SOLIDWORKS PART (.sldprt)
format: sldprt  version: not decoded by parser v0  size: 238,592 bytes
history: native  units: mm
features: sketch x4, fillet x4, extrude x3, plane x2, material x1, shell x1, cut_extrude x1 (+13 scaffold rows collapsed)
feature tree (29):
  scaffold x13  (default folders/planes/origin — collapsed)
  material  "ABS"
  plane  "Plane1"
  sketch  "Sketch1"  dims[D1=50.0mm D2=110.0mm]
  extrude  "Boss-Extrude1"  Depth=5.08mm
  shell  "Shell1"  Thickness=3.048mm
  sketch  "Sketch4"  dims[c1.D1=5.2832mm c1.D2=5.2832mm c2.D1=93.0mm c2.D2=2.64mm c2.D3=3.5mm c2.D4=2.64mm c2.D5=2.64mm c3.D1=3.5mm c3.D2=3.5mm c3.D4=3.5mm]
  cut_extrude  "Cut-Extrude1"  [1 undecoded]
  fillet  "Fillet1"  Radius=3.5052mm
  plane  "Plane2"
  sketch  "Sketch6"  dims[D1=2.032mm]
  extrude  "Boss-Extrude3"  Depth=2.54mm
  sketch  "Sketch7"
  extrude  "Boss-Extrude4"  Depth=1.524mm
  fillet  "Fillet2"  Radius=2.54mm
  fillet  "Fillet3"  Radius=0.508mm
  fillet  "Fillet4"  Radius=0.508mm
decode coverage: 11 of 13 modeling features carry decoded parameters
note: 1 parameter value undecoded
note: suppression state not decoded; provenance and decode notes live in map.json
